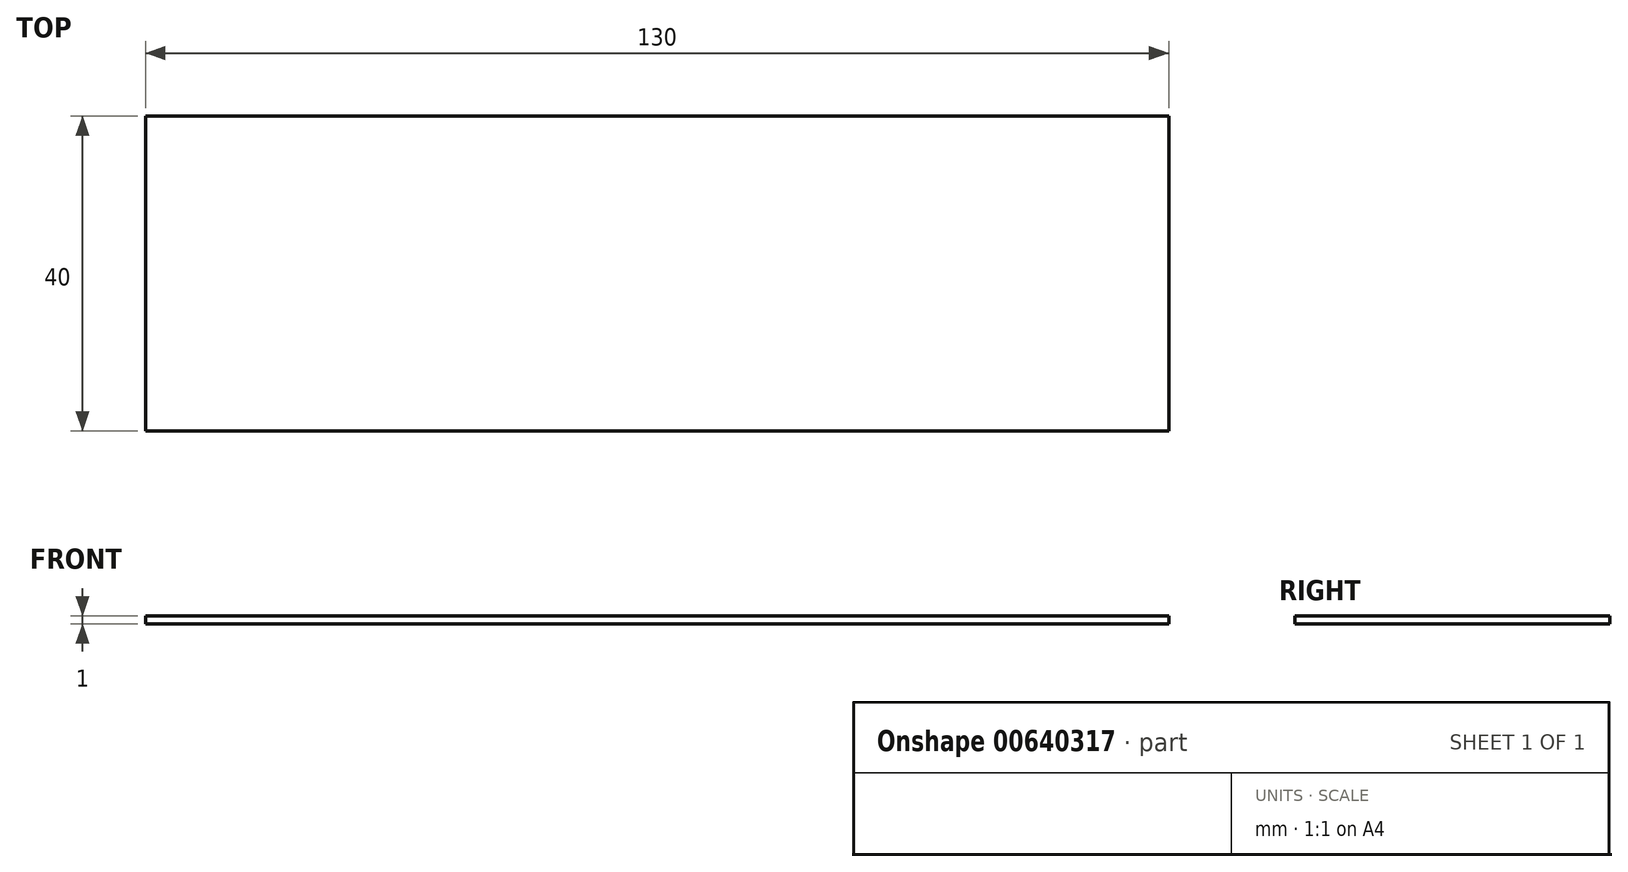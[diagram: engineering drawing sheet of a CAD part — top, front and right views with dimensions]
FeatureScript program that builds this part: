
annotation { "Feature Type Name" : "Feature", "Feature Type Description" : "" }
export const myFeature = defineFeature(function(context is Context, id is Id, definition is map)
    precondition{}
    {
        {
            var Q0;
            Q0=qCreatedBy(makeId("Top.planeOp"),FACE);
            var sketch = newSketch(context, id + "F0", { "sketchPlane" : qUnion([Q0])});
            skLineSegment(sketch, "E0.bottom", {"start": v(65, -20) * mm, "end": v(-65, -20) * mm});
            skLineSegment(sketch, "E0.top", {"start": v(65, 20) * mm, "end": v(-65, 20) * mm});
            skLineSegment(sketch, "E0.left", {"start": v(65, -20) * mm, "end": v(65, 20) * mm});
            skLineSegment(sketch, "E0.right", {"start": v(-65, -20) * mm, "end": v(-65, 20) * mm});
            skPoint(sketch, "E0.middle", {"position": v(0, 0) * mm});
            skSolve(sketch);
        }
        {
            var Q0;
            Q0=makeQuery(id+"F0.imprint","IMPRINT",FACE,{"disambiguationData":[TD([[makeQuery(id+"F0.imprint","IMPRINT",EDGE,{"derivedFrom":sQuery(id+"F0.wireOp",EDGE,"E0.bottom")}),-1.0]])]});
            extrude(context, id + "F1", {"entities" : qUnion([Q0]), "depth" : 1 * mm, "offsetDistance" : 25 * mm});
        }
    });
